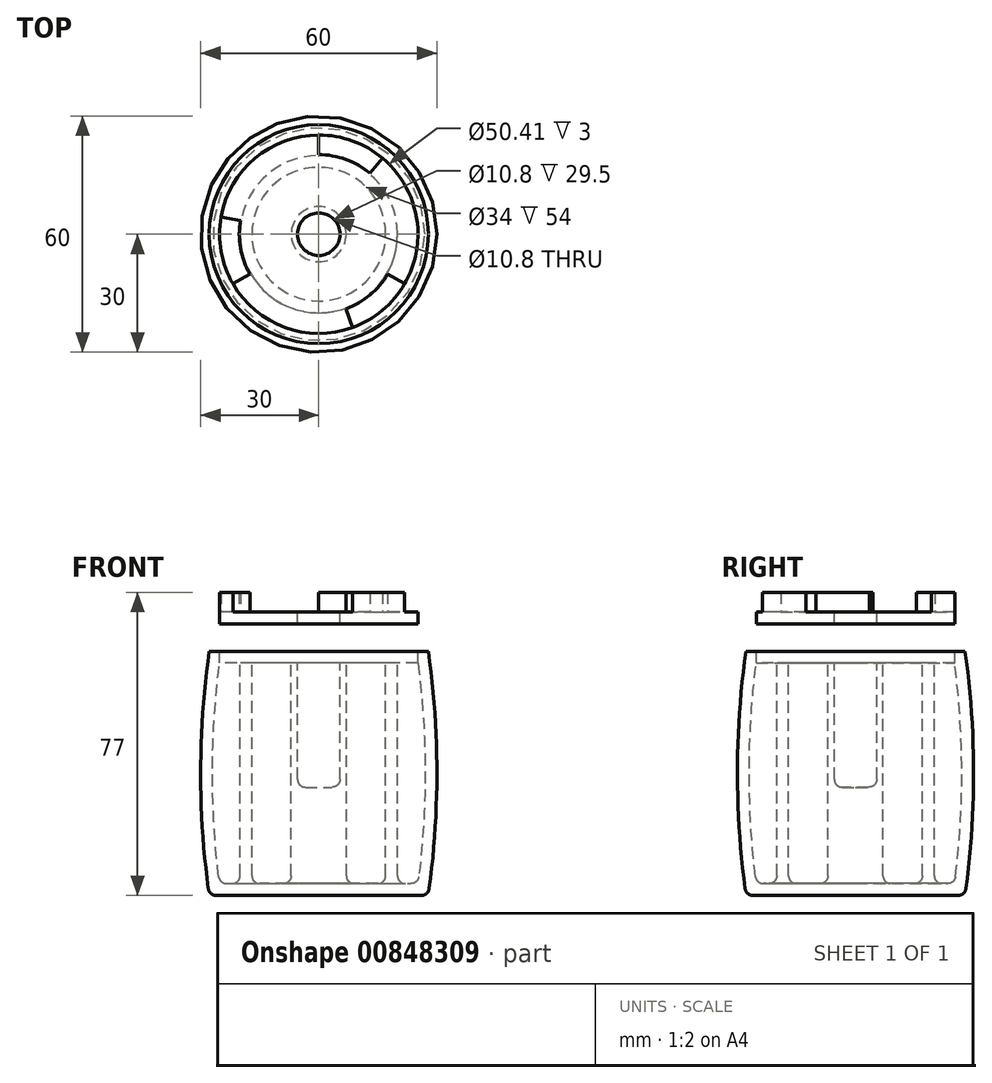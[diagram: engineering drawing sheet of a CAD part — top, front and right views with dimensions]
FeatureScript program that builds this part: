
annotation { "Feature Type Name" : "Feature", "Feature Type Description" : "" }
export const myFeature = defineFeature(function(context is Context, id is Id, definition is map)
    precondition{}
    {
        {
            var Q0;
            Q0=qCreatedBy(makeId("Front.planeOp"),FACE);
            var sketch = newSketch(context, id + "F0", { "sketchPlane" : qUnion([Q0])});
            skLineSegment(sketch, "E0", {"start": v(0, 0) * mm, "end": v(-27.82, 0) * mm});
            skArc(sketch, "E1", {"start": v(-27.82, 62) * mm, "mid": v(-30, 31) * mm, "end": v(-27.82, 0) * mm});
            skLineSegment(sketch, "E2", {"start": v(-17, 59) * mm, "end": v(-17, 3) * mm});
            skLineSegment(sketch, "E3", {"start": v(-5.4, 27.5) * mm, "end": v(0, 27.5) * mm});
            skLineSegment(sketch, "E4", {"start": v(-25.2, 3) * mm, "end": v(-20, 3) * mm});
            skLineSegment(sketch, "E5", {"start": v(-20, 3) * mm, "end": v(-20, 59) * mm});
            skArc(sketch, "E6", {"start": v(-25.2, 59) * mm, "mid": v(-27, 31) * mm, "end": v(-25.2, 3) * mm});
            skLineSegment(sketch, "E7", {"start": v(-7, 3) * mm, "end": v(-17, 3) * mm});
            skLineSegment(sketch, "E8", {"start": v(-17, 59) * mm, "end": v(-20, 59) * mm});
            skLineSegment(sketch, "E9", {"start": v(-5.4, 59) * mm, "end": v(-7, 59) * mm});
            skPoint(sketch, "E10", {"position": v(0, 32.5) * mm});
            skLineSegment(sketch, "E11", {"start": v(-25.2, 59) * mm, "end": v(-25.2, 62) * mm});
            skLineSegment(sketch, "E12", {"start": v(-25.2, 62) * mm, "end": v(-27.82, 62) * mm});
            skLineSegment(sketch, "E13", {"start": v(0, 27.5) * mm, "end": v(0, 0) * mm});
            skLineSegment(sketch, "E14", {"start": v(-5.4, 59) * mm, "end": v(-5.4, 27.5) * mm});
            skLineSegment(sketch, "E15", {"start": v(-7, 59) * mm, "end": v(-7, 3) * mm});
            skLineSegment(sketch, "E16", {"start": v(-7, 59) * mm, "end": v(-17, 59) * mm, "construction": true});
            skLineSegment(sketch, "E17", {"start": v(-20, 59) * mm, "end": v(-25.2, 59) * mm, "construction": true});
            skLineSegment(sketch, "E18", {"start": v(-27.82, 62) * mm, "end": v(-27.82, 0) * mm, "construction": true});
            skSolve(sketch);
        }
        {
            var Q0;
            Q0=qCreatedBy(makeId("Front.planeOp"),FACE);
            var sketch = newSketch(context, id + "F1", { "sketchPlane" : qUnion([Q0])});
            skLineSegment(sketch, "E19", {"start": v(-5.4, 69) * mm, "end": v(-25.2, 69) * mm});
            skLineSegment(sketch, "E20", {"start": v(-25.2, 69) * mm, "end": v(-25.2, 72) * mm});
            skLineSegment(sketch, "E21", {"start": v(-25.2, 72) * mm, "end": v(-5.4, 72) * mm});
            skLineSegment(sketch, "E22", {"start": v(-5.4, 72) * mm, "end": v(-5.4, 69) * mm});
            skPoint(sketch, "E23.0", {"position": v(-5.4, 59) * mm});
            skPoint(sketch, "E24.0", {"position": v(-25.2, 62) * mm});
            skSolve(sketch);
        }
        {
            var Q0;
            Q0=makeQuery(id+"F0.imprint","IMPRINT",FACE,{"disambiguationData":[TD([[makeQuery(id+"F0.imprint","IMPRINT",EDGE,{"derivedFrom":sQuery(id+"F0.wireOp",EDGE,"E0")}),-1.0]])]});
            var Q1;
            Q1=sQuery(id+"F0.wireOp",EDGE,"E13");
            revolve(context, id + "F2", {"surfaceOperationType" : NewSurfaceOperationType.NEW, "entities" : qUnion([Q0]), "axis" : qUnion([Q1]), "revolveType" : RevolveType.FULL});
        }
        {
            var Q0;
            Q0=makeQuery(id+"F1.imprint","IMPRINT",FACE,{"disambiguationData":[TD([[makeQuery(id+"F1.imprint","IMPRINT",EDGE,{"derivedFrom":sQuery(id+"F1.wireOp",EDGE,"E19")}),-1.0]])]});
            var Q1;
            Q1=sQuery(id+"F0.wireOp",EDGE,"E13");
            revolve(context, id + "F3", {"surfaceOperationType" : NewSurfaceOperationType.NEW, "entities" : qUnion([Q0]), "axis" : qUnion([Q1]), "revolveType" : RevolveType.FULL});
        }
        {
            var Q0;
            Q0=makeQuery(id+"F2.opRevolve","SWEPT_EDGE",EDGE,{"disambiguationData":[OSD([sQuery(id+"F0.wireOp",EDGE,"zfuqpYvi-nD6G-48Wu-hoye-4oUvRpUNeBjX"),sQuery(id+"F0.wireOp",EDGE,"E3")])]});
            var Q1;
            Q1=makeQuery(id+"F2.opRevolve","SWEPT_EDGE",EDGE,{"disambiguationData":[OSD([sQuery(id+"F0.wireOp",EDGE,"73oQLxVT-LSWg-F1Ge-i0z1-ve6tOWOdIWX1"),sQuery(id+"F0.wireOp",EDGE,"E7")])]});
            var Q2;
            Q2=makeQuery(id+"F2.opRevolve","SWEPT_EDGE",EDGE,{"disambiguationData":[OSD([sQuery(id+"F0.wireOp",EDGE,"E2"),sQuery(id+"F0.wireOp",EDGE,"E7")])]});
            var Q3;
            Q3=makeQuery(id+"F2.opRevolve","SWEPT_EDGE",EDGE,{"disambiguationData":[OSD([sQuery(id+"F0.wireOp",EDGE,"E4"),sQuery(id+"F0.wireOp",EDGE,"E6")])]});
            var Q4;
            Q4=makeQuery(id+"F2.opRevolve","SWEPT_EDGE",EDGE,{"disambiguationData":[OSD([sQuery(id+"F0.wireOp",EDGE,"E4"),sQuery(id+"F0.wireOp",EDGE,"E5")])]});
            fillet(context, id + "F4", {"entities" : qUnion([Q0, Q1, Q2, Q3, Q4]), "radius" : 2 * mm, "tangentPropagation" : true, "allowEdgeOverflow" : false});
        }
        {
            var Q0;
            Q0=makeQuery(id+"F2.opRevolve","SWEPT_EDGE",EDGE,{"disambiguationData":[OSD([sQuery(id+"F0.wireOp",EDGE,"E0"),sQuery(id+"F0.wireOp",EDGE,"E1")])]});
            fillet(context, id + "F5", {"entities" : qUnion([Q0]), "radius" : 2 * mm, "tangentPropagation" : true, "allowEdgeOverflow" : false});
        }
        {
            var Q0;
            Q0=makeQuery(id+"F3.opRevolve","SWEPT_FACE",FACE,{"disambiguationData":[OSD([sQuery(id+"F1.wireOp",EDGE,"E21")])]});
            var sketch = newSketch(context, id + "F6", { "sketchPlane" : qUnion([Q0])});
            skPoint(sketch, "E25.0", {"position": v(0, 0) * mm});
            skLineSegment(sketch, "E26", {"start": v(0, 20.2) * mm, "end": v(0, 25.2) * mm});
            skLineSegment(sketch, "E27", {"start": v(0, 0) * mm, "end": v(12.99, 15.48) * mm, "construction": true});
            skArc(sketch, "E28", {"start": v(12.99, 15.48) * mm, "mid": v(6.9, 18.98) * mm, "end": v(0, 20.2) * mm});
            skLineSegment(sketch, "E29", {"start": v(12.99, 15.48) * mm, "end": v(16.2, 19.3) * mm});
            skArc(sketch, "E30", {"start": v(0, 25.2) * mm, "mid": v(-8.62, -23.68) * mm, "end": v(16.2, 19.3) * mm, "construction": true});
            skArc(sketch, "E31", {"start": v(16.2, 19.3) * mm, "mid": v(8.62, 23.68) * mm, "end": v(0, 25.2) * mm});
            skLineSegment(sketch, "E32.1.0", {"start": v(-17.5, -10.1) * mm, "end": v(-21.83, -12.6) * mm});
            skArc(sketch, "E32.1.1", {"start": v(-24.82, 4.38) * mm, "mid": v(-24.82, -4.38) * mm, "end": v(-21.83, -12.6) * mm});
            skLineSegment(sketch, "E32.1.2", {"start": v(-19.9, 3.5) * mm, "end": v(-24.82, 4.38) * mm});
            skArc(sketch, "E32.1.3", {"start": v(-19.9, 3.5) * mm, "mid": v(-19.9, -3.5) * mm, "end": v(-17.5, -10.1) * mm});
            skLineSegment(sketch, "E32.2.0", {"start": v(17.5, -10.1) * mm, "end": v(21.83, -12.6) * mm});
            skArc(sketch, "E32.2.1", {"start": v(8.62, -23.68) * mm, "mid": v(16.2, -19.3) * mm, "end": v(21.83, -12.6) * mm});
            skLineSegment(sketch, "E32.2.2", {"start": v(6.9, -18.98) * mm, "end": v(8.62, -23.68) * mm});
            skArc(sketch, "E32.2.3", {"start": v(6.9, -18.98) * mm, "mid": v(12.99, -15.48) * mm, "end": v(17.5, -10.1) * mm});
            skSolve(sketch);
        }
        {
            var Q0;
            Q0=makeQuery(id+"F6.imprint","IMPRINT",FACE,{"disambiguationData":[TD([[makeQuery(id+"F6.imprint","IMPRINT",EDGE,{"derivedFrom":sQuery(id+"F6.wireOp",EDGE,"E26")}),-1.0]])]});
            var Q1;
            Q1=makeQuery(id+"F6.imprint","IMPRINT",FACE,{"disambiguationData":[TD([[makeQuery(id+"F6.imprint","IMPRINT",EDGE,{"derivedFrom":sQuery(id+"F6.wireOp",EDGE,"E32.2.0")}),-1.0]])]});
            var Q2;
            Q2=makeQuery(id+"F6.imprint","IMPRINT",FACE,{"disambiguationData":[TD([[makeQuery(id+"F6.imprint","IMPRINT",EDGE,{"derivedFrom":sQuery(id+"F6.wireOp",EDGE,"E32.1.0")}),-1.0]])]});
            extrude(context, id + "F7", {"entities" : qUnion([Q0, Q1, Q2]), "operationType" : NewBodyOperationType.ADD, "depth" : 5 * mm, "offsetDistance" : 25 * mm});
        }
    });
